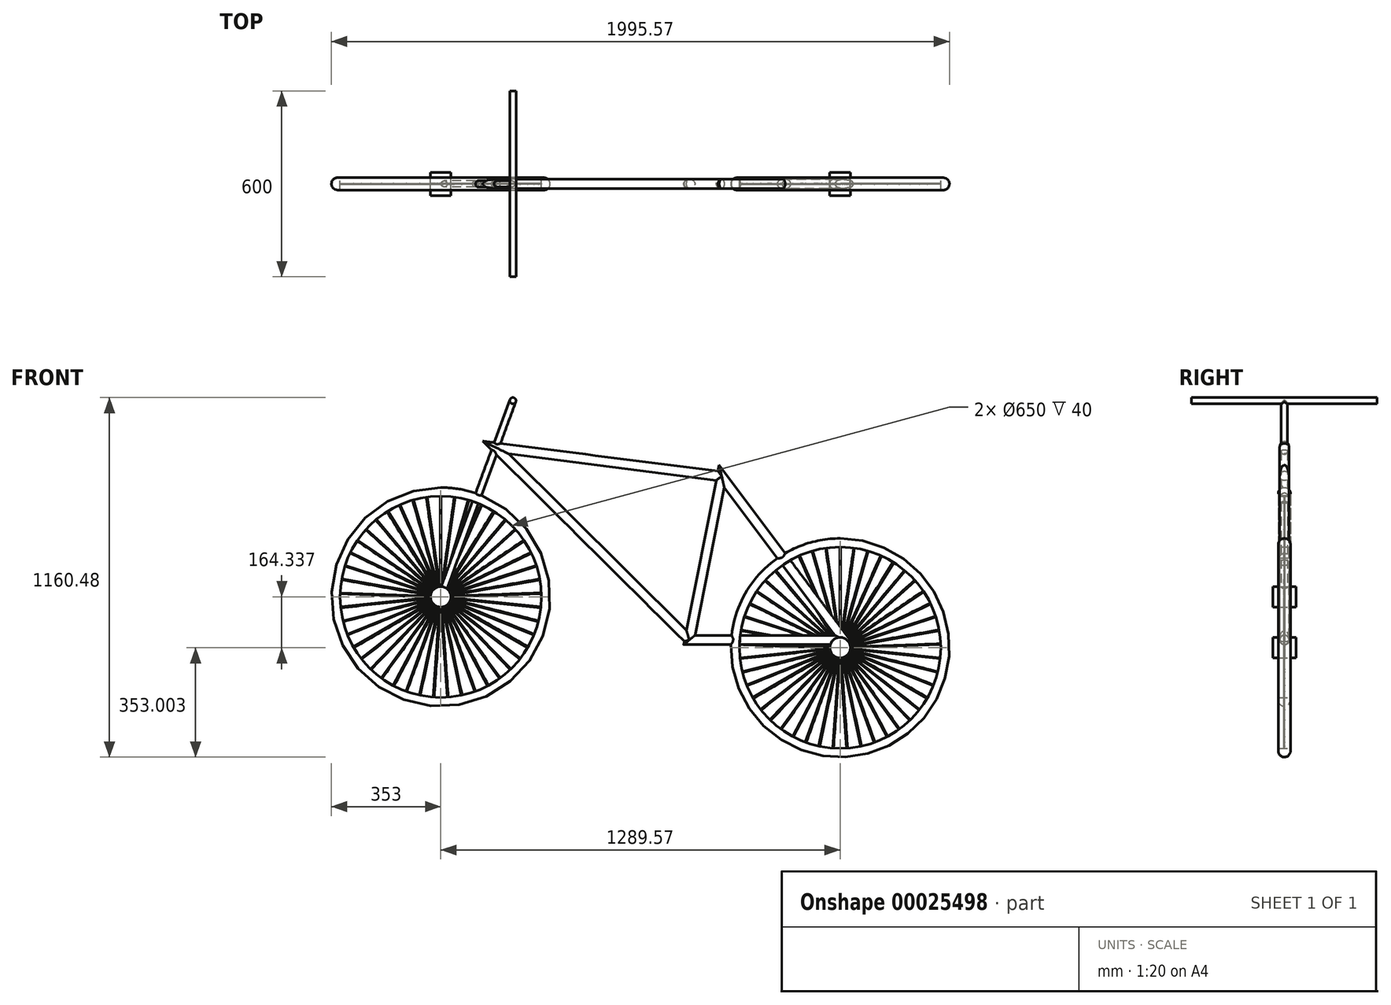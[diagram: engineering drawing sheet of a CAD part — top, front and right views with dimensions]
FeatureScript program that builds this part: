
annotation { "Feature Type Name" : "Feature", "Feature Type Description" : "" }
export const myFeature = defineFeature(function(context is Context, id is Id, definition is map)
    precondition{}
    {
        {
            var Q0;
            Q0=qCreatedBy(makeId("Front.planeOp"),FACE);
            var sketch = newSketch(context, id + "F0", { "sketchPlane" : qUnion([Q0])});
            skLineSegment(sketch, "E0", {"start": v(0, 0) * mm, "end": v(0, 325) * mm, "construction": true});
            skSolve(sketch);
        }
        {
            var Q0;
            Q0=qCreatedBy(makeId("Top.planeOp"),FACE);
            var sketch = newSketch(context, id + "F1", { "sketchPlane" : qUnion([Q0])});
            skLineSegment(sketch, "E1", {"start": v(0, 0) * mm, "end": v(0, -52.7) * mm, "construction": true});
            skSolve(sketch);
        }
        {
            var Q0;
            Q0=qCreatedBy(makeId("Right.planeOp"),FACE);
            var sketch = newSketch(context, id + "F2", { "sketchPlane" : qUnion([Q0])});
            skPoint(sketch, "E2.0", {"position": v(0, 325) * mm});
            skLineSegment(sketch, "E3", {"start": v(-20, 325) * mm, "end": v(20, 325) * mm});
            skLineSegment(sketch, "E4", {"start": v(20, 325) * mm, "end": v(20, 333) * mm});
            skLineSegment(sketch, "E5", {"start": v(-20, 333) * mm, "end": v(-20, 325) * mm});
            skArc(sketch, "E6", {"start": v(20, 333) * mm, "mid": v(0, 353) * mm, "end": v(-20, 333) * mm});
            skSolve(sketch);
        }
        {
            var Q0;
            Q0=makeQuery(id+"F2.imprint","IMPRINT",FACE,{"disambiguationData":[TD([[makeQuery(id+"F2.imprint","IMPRINT",EDGE,{"derivedFrom":sQuery(id+"F2.wireOp",EDGE,"E3")}),1.0]])]});
            var Q1;
            Q1=sQuery(id+"F1.wireOp",EDGE,"E1");
            revolve(context, id + "F3", {"entities" : qUnion([Q0]), "axis" : qUnion([Q1]), "revolveType" : RevolveType.FULL});
        }
        {
            var Q0;
            Q0=qCreatedBy(makeId("Front.planeOp"),FACE);
            var sketch = newSketch(context, id + "F4", { "sketchPlane" : qUnion([Q0])});
            skCircle(sketch, "E7", {"center": v(0, 0) * mm, "radius": 33.31 * mm});
            skSolve(sketch);
        }
        {
            var Q0;
            Q0=makeQuery(id+"F4.imprint","IMPRINT",FACE,{"disambiguationData":[TD([[makeQuery(id+"F4.imprint","IMPRINT",EDGE,{"derivedFrom":sQuery(id+"F4.wireOp",EDGE,"E7")}),1.0]])]});
            extrude(context, id + "F5", {"entities" : qUnion([Q0]), "endBound" : BoundingType.SYMMETRIC, "depth" : 75 * mm});
        }
        {
            var Q0;
            Q0=qCreatedBy(makeId("Top.planeOp"),FACE);
            cPlane(context, id + "F6", {"entities" : qUnion([Q0]), "cplaneType" : CPlaneType.OFFSET, "offset" : 150 * mm, "width" : 150 * mm, "height" : 150 * mm});
        }
        {
            var Q0;
            Q0=qCreatedBy(id+"F6.planeOp",FACE);
            var sketch = newSketch(context, id + "F7", { "sketchPlane" : qUnion([Q0])});
            skCircle(sketch, "E8", {"center": v(0, 0) * mm, "radius": 1.5 * mm});
            skSolve(sketch);
        }
        {
            var Q0;
            Q0=makeQuery(id+"F7.imprint","IMPRINT",FACE,{"disambiguationData":[TD([[makeQuery(id+"F7.imprint","IMPRINT",EDGE,{"derivedFrom":sQuery(id+"F7.wireOp",EDGE,"E8")}),1.0]])]});
            extrude(context, id + "F8", {"entities" : qUnion([Q0]), "endBound" : BoundingType.UP_TO_NEXT, "depth" : 1000 * mm, "hasSecondDirection" : true, "secondDirectionBound" : SecondDirectionBoundingType.UP_TO_NEXT, "secondDirectionOppositeDirection" : true, "secondDirectionDepth" : 25 * mm});
        }
        {
            var Q0;
            Q0=makeQuery(id+"F8.opExtrude","SWEPT_BODY",BODY,{"disambiguationData":[OSD([sQuery(id+"F7.wireOp",EDGE,"E8")])]});
            var Q1;
            Q1=sQuery(id+"F1.wireOp",EDGE,"E1");
            circularPattern(context, id + "F9", {"operationType" : NewBodyOperationType.ADD, "entities" : qUnion([Q0]), "axis" : qUnion([Q1]), "angle" : 8 * degree, "instanceCount" : 45});
        }
        {
            var Q0;
            Q0=qCreatedBy(makeId("Front.planeOp"),FACE);
            var sketch = newSketch(context, id + "F10", { "sketchPlane" : qUnion([Q0])});
            skPoint(sketch, "E9.0", {"position": v(0, 0) * mm});
            skLineSegment(sketch, "E10", {"start": v(177.4, 482.06) * mm, "end": v(802.72, -139.16) * mm});
            skLineSegment(sketch, "E11", {"start": v(177.4, 482.06) * mm, "end": v(907.3, 389.05) * mm});
            skLineSegment(sketch, "E12", {"start": v(907.3, 389.05) * mm, "end": v(802.72, -139.16) * mm});
            skLineSegment(sketch, "E13", {"start": v(1302.72, -139.16) * mm, "end": v(907.3, 389.05) * mm});
            skLineSegment(sketch, "E14", {"start": v(802.72, -139.16) * mm, "end": v(1302.72, -139.16) * mm});
            skLineSegment(sketch, "E15", {"start": v(0, 0) * mm, "end": v(232.99, 633.14) * mm});
            skPoint(sketch, "E16", {"position": v(177.4, 482.06) * mm});
            skSolve(sketch);
        }
        {
            var Q0;
            Q0=makeQuery(id+"F3.opRevolve","SWEPT_BODY",BODY,{"disambiguationData":[OSD([sQuery(id+"F2.wireOp",EDGE,"E3"),sQuery(id+"F2.wireOp",EDGE,"E4"),sQuery(id+"F2.wireOp",EDGE,"E5"),sQuery(id+"F2.wireOp",EDGE,"E6")])]});
            var Q1;
            Q1=sQuery(id+"F10.wireOp",EDGE,"E11");
            transform(context, id + "F11", {"entities" : qUnion([Q0]), "transformType" : TransformType.TRANSLATION_DISTANCE, "transformDirection" : qUnion([Q1]), "distance" : 1300 * mm, "makeCopy" : true});
        }
        {
            var Q0;
            Q0=sQuery(id+"F10.wireOp",EDGE,"E12");
            var Q1;
            Q1=sQuery(id+"F10.wireOp",VERTEX,"E13.end");
            cPlane(context, id + "F12", {"entities" : qUnion([Q0, Q1]), "cplaneType" : CPlaneType.LINE_POINT, "offset" : 150 * mm, "width" : 150 * mm, "height" : 150 * mm});
        }
        {
            var Q0;
            Q0=qCreatedBy(id+"F12.planeOp",FACE);
            var sketch = newSketch(context, id + "F13", { "sketchPlane" : qUnion([Q0])});
            skPoint(sketch, "E17.0", {"position": v(814.46, 0) * mm});
            skCircle(sketch, "E18", {"center": v(814.46, 0) * mm, "radius": 15 * mm});
            skSolve(sketch);
        }
        {
            var Q0;
            Q0=makeQuery(id+"F13.imprint","IMPRINT",FACE,{"disambiguationData":[TD([[makeQuery(id+"F13.imprint","IMPRINT",EDGE,{"derivedFrom":sQuery(id+"F13.wireOp",EDGE,"E18")}),1.0]])]});
            var Q1;
            Q1=sQuery(id+"F10.wireOp",EDGE,"E12");
            var Q2;
            Q2=sQuery(id+"F10.wireOp",EDGE,"E14");
            var Q3;
            Q3=sQuery(id+"F10.wireOp",EDGE,"E13");
            sweep(context, id + "F14", {"operationType" : NewBodyOperationType.ADD, "profiles" : qUnion([Q0]), "path" : qUnion([Q1, Q2, Q3])});
        }
        {
            var Q0;
            Q0=sQuery(id+"F10.wireOp",EDGE,"E11");
            var Q1;
            Q1=sQuery(id+"F10.wireOp",VERTEX,"E13.end");
            cPlane(context, id + "F15", {"entities" : qUnion([Q0, Q1]), "cplaneType" : CPlaneType.LINE_POINT, "offset" : 150 * mm, "width" : 150 * mm, "height" : 150 * mm});
        }
        {
            var Q0;
            Q0=qCreatedBy(id+"F15.planeOp",FACE);
            var sketch = newSketch(context, id + "F16", { "sketchPlane" : qUnion([Q0])});
            skPoint(sketch, "E19.0", {"position": v(0, 500.62) * mm});
            skCircle(sketch, "E20", {"center": v(0, 500.62) * mm, "radius": 15 * mm});
            skSolve(sketch);
        }
        {
            var Q0;
            Q0 = qSketchRegion(id + "F16", true);
            var Q1;
            Q1=sQuery(id+"F10.wireOp",EDGE,"E11");
            var Q2;
            Q2=sQuery(id+"F10.wireOp",EDGE,"E10");
            sweep(context, id + "F17", {"operationType" : NewBodyOperationType.ADD, "profiles" : qUnion([Q0]), "path" : qUnion([Q1, Q2])});
        }
        {
            var Q0;
            Q0=sQuery(id+"F10.wireOp",VERTEX,"E15.end");
            var Q1;
            Q1=sQuery(id+"F10.wireOp",EDGE,"E15");
            cPlane(context, id + "F18", {"entities" : qUnion([Q0, Q1]), "cplaneType" : CPlaneType.LINE_POINT, "offset" : 150 * mm, "width" : 150 * mm, "height" : 150 * mm});
        }
        {
            var Q0;
            Q0=qCreatedBy(id+"F18.planeOp",FACE);
            var sketch = newSketch(context, id + "F19", { "sketchPlane" : qUnion([Q0])});
            skPoint(sketch, "E21.0", {"position": v(0, 0) * mm});
            skCircle(sketch, "E22", {"center": v(0, 0) * mm, "radius": 10 * mm});
            skSolve(sketch);
        }
        {
            var Q0;
            Q0=makeQuery(id+"F19.imprint","IMPRINT",FACE,{"disambiguationData":[TD([[makeQuery(id+"F19.imprint","IMPRINT",EDGE,{"derivedFrom":sQuery(id+"F19.wireOp",EDGE,"E22")}),1.0]])]});
            var Q1;
            Q1=sQuery(id+"F10.wireOp",EDGE,"E15");
            sweep(context, id + "F20", {"operationType" : NewBodyOperationType.ADD, "profiles" : qUnion([Q0]), "path" : qUnion([Q1])});
        }
        {
            var Q0;
            Q0=makeQuery(id+"F20.opSweep","CAP_FACE",FACE,{"disambiguationData":[OSD([sQuery(id+"F10.wireOp",VERTEX,"E15.end"),sQuery(id+"F19.wireOp",EDGE,"E22")])],"isStart":true});
            var sketch = newSketch(context, id + "F21", { "sketchPlane" : qUnion([Q0])});
            skLineSegment(sketch, "E23", {"start": v(0, 300) * mm, "end": v(0, -300) * mm});
            skPoint(sketch, "E24", {"position": v(0, 0) * mm});
            skSolve(sketch);
        }
        {
            var Q0;
            Q0=sQuery(id+"F21.wireOp",EDGE,"E23");
            var Q1;
            Q1=sQuery(id+"F21.wireOp",VERTEX,"E23.start");
            cPlane(context, id + "F22", {"entities" : qUnion([Q0, Q1]), "cplaneType" : CPlaneType.LINE_POINT, "offset" : 150 * mm, "width" : 150 * mm, "height" : 150 * mm});
        }
        {
            var Q0;
            Q0=qCreatedBy(id+"F22.planeOp",FACE);
            var sketch = newSketch(context, id + "F23", { "sketchPlane" : qUnion([Q0])});
            skCircle(sketch, "E25", {"center": v(232.99, 633.14) * mm, "radius": 10 * mm});
            skSolve(sketch);
        }
        {
            var Q0;
            Q0=makeQuery(id+"F23.imprint","IMPRINT",FACE,{"disambiguationData":[TD([[makeQuery(id+"F23.imprint","IMPRINT",EDGE,{"derivedFrom":sQuery(id+"F23.wireOp",EDGE,"E25")}),1.0]])]});
            var Q1;
            Q1=sQuery(id+"F21.wireOp",EDGE,"E23");
            sweep(context, id + "F24", {"operationType" : NewBodyOperationType.ADD, "profiles" : qUnion([Q0]), "path" : qUnion([Q1])});
        }
    });
